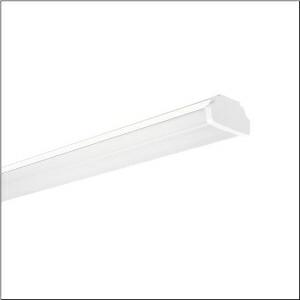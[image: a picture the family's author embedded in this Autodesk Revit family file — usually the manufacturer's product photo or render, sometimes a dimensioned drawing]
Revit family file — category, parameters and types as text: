
# Revit family: modario_31_gen_2_53bm812mv485c2_3aa5
name_source: partatom
category: Lighting Fixtures
units: mm (PartAtom-declared; Revit-internal decimal feet)

## family parameters
Cut with Voids When Loaded = No
Host = Face
Light Source = No
Part Type = Normal
Room Calculation Point = No
Round Connector Dimension = Use Diameter
Shared = No

## types (1)
- --- (1 x LED, 8950 lm, 48.2 W, 4000K)
    Apparent Load = 48 VA
    CIE Flux Codes = 47 80 95 93 100
    Color Rendering = 80
    Color Temperature = 4000K
    Default Elevation = 1800 mm
    Description = Modario 31 Gen.2, luminaire insert, of sheet steel, coil coated, white, length: 1.495mm, width: 81mm, height: 82mm, 5x system unit, system units: 299mm, LED rated luminous flux: 8.950lm, light colour: 840, SDCM (Standard Deviation of Colour Matching)MacAdam ≤ 3 SDCM (initial), control gear: ON/OFF Multilumen, control gear: ECG, with plug, 3-pole, with phase selection, mains connection: 220..240V, AC, 50/60Hz, rated input power: 48W, through-wiring accessed according to module size, primary optical cover: cover, of PMMA, light emission: direct distribution, primary light characteristic: symmetric, protection rating (complete): IP20, protection rating (LED compartment): IP50, insulation class (complete): insulation class I (protective earthing), certification: CE, ENEC, VDE, UKCA, impact resistance: IK03, permissible ambient temperature for indoor applications: -35..+50°C, corresponds to IFS (International Featured Standards) requirements for safety and quality in the food industry, reducing of maximum allowable ambient temperature of 5°C with ceiling mounting, IP40 when using the optional accessory 5TP9018, packaging unit: 1 piece
    Height = 92 mm
    Lamp = 1 x LED
    Lamp Light Flux = 8950 lm
    Lamp Power = 48.2 W
    Lamp count = 1
    Length = 1495 mm
    Luminous efficacy = 186 lm/W
    Manufacturer = Siteco
    ModVariant = No
    Model = 53BM812MV485C2
    Mounting Place = Ceiling
    Mounting Type = Pendant
    Number of Poles = 1
    OnlyDefault = Yes
    Power Factor = 1
    Product Name = Modario 31 Gen.2
    Product group = luminaire insert | ceiling pendant
    ProductGroupID = 901
    Protection Class = Protection class I
    Protection Degree = IP 20
    RLX_Detail_Level = 1
    RLX_Emergency_Light_Flux = 0 lm
    RLX_Emergency_Type = 0
    RLX_Emergency_Type_DB = No
    RlxData = <blob elided: 40077 chars, md5=8b236993>
    Socket = socket
    Standby Power = 0 W
    System Light Flux = 8950 lm
    System Power = 48 W
    Type Comments = factory setting: luminous flux: 100 % | (A | C | E) | 112 mA
    Type Image = l_1341886.jpg
    URL = http://relux.com
    VarID = @adj_040755
    Voltage = 0 V
    Weight = 0.00 kg
    Width = 81 mm

## geometry (parser evidence)
native form markers: Blend x4, Sweep x13
no freeform markers — native parametric forms only
